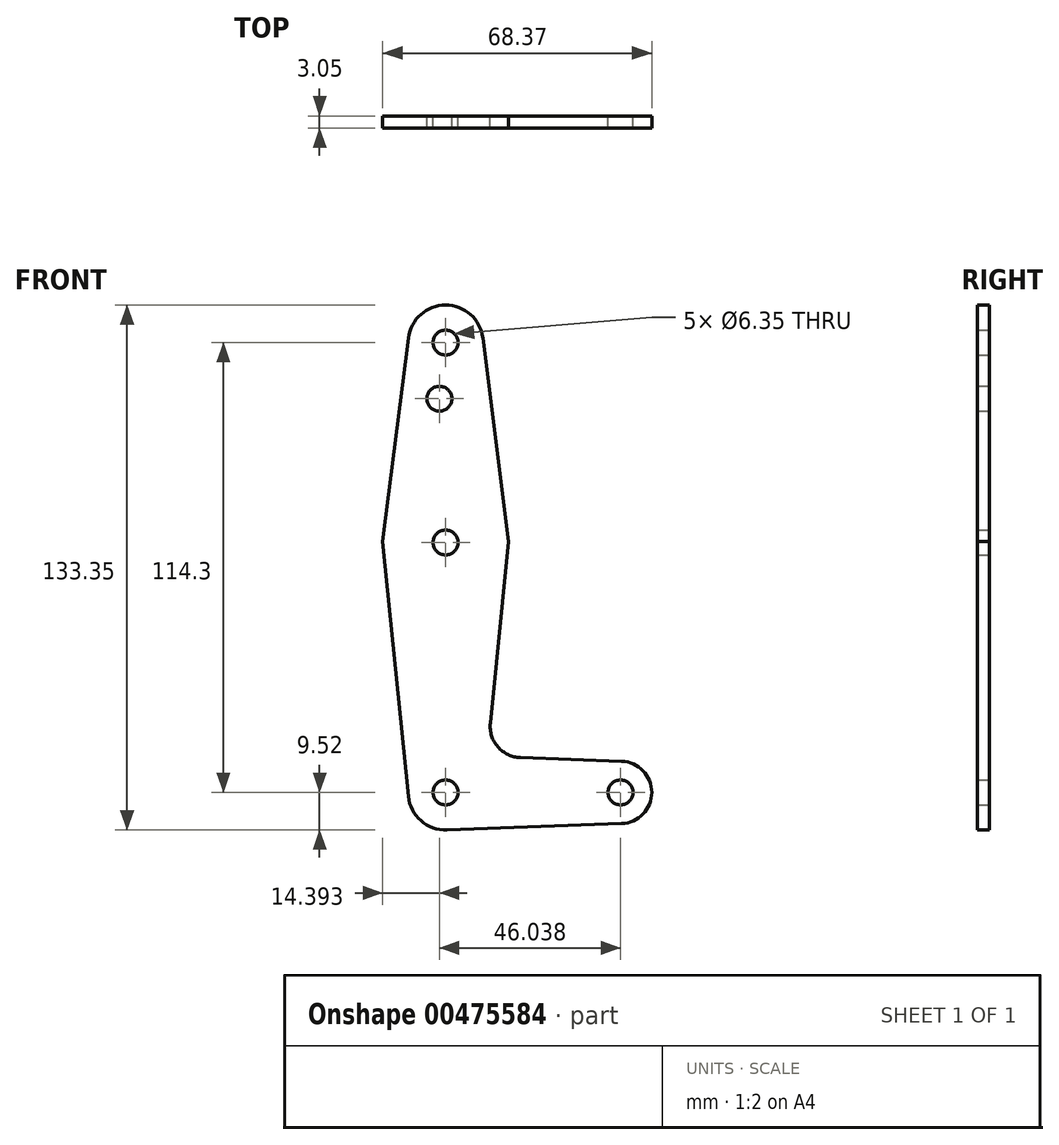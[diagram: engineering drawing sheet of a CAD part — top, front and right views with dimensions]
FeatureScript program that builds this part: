
annotation { "Feature Type Name" : "Feature", "Feature Type Description" : "" }
export const myFeature = defineFeature(function(context is Context, id is Id, definition is map)
    precondition{}
    {
        {
            var Q0;
            Q0=qCreatedBy(makeId("Front.planeOp"),FACE);
            var sketch = newSketch(context, id + "F0", { "sketchPlane" : qUnion([Q0])});
            skLineSegment(sketch, "E0", {"start": v(0, 0) * mm, "end": v(0, 114.3) * mm, "construction": true});
            skLineSegment(sketch, "E1", {"start": v(0, 0) * mm, "end": v(44.45, 0) * mm, "construction": true});
            skCircle(sketch, "E2", {"center": v(0, 114.3) * mm, "radius": 9.53 * mm});
            skCircle(sketch, "E3", {"center": v(0, 63.5) * mm, "radius": 15.88 * mm});
            skCircle(sketch, "E4", {"center": v(0, 0) * mm, "radius": 9.53 * mm});
            skCircle(sketch, "E5", {"center": v(44.45, 0) * mm, "radius": 7.94 * mm});
            skLineSegment(sketch, "E6", {"start": v(0.34, -9.52) * mm, "end": v(44.73, -7.93) * mm});
            skLineSegment(sketch, "E7", {"start": v(18.97, 8.85) * mm, "end": v(44.73, 7.93) * mm});
            skLineSegment(sketch, "E8", {"start": v(-15.98, 63.7) * mm, "end": v(-9.48, -0.95) * mm});
            skLineSegment(sketch, "E9", {"start": v(15.98, 63.7) * mm, "end": v(11.34, 17.6) * mm});
            skLineSegment(sketch, "E10", {"start": v(-9.45, 115.5) * mm, "end": v(-15.98, 63.7) * mm});
            skLineSegment(sketch, "E11", {"start": v(9.45, 115.5) * mm, "end": v(15.98, 63.7) * mm});
            skCircle(sketch, "E12", {"center": v(0, 114.3) * mm, "radius": 3.18 * mm});
            skCircle(sketch, "E13", {"center": v(0, 0) * mm, "radius": 3.18 * mm});
            skCircle(sketch, "E14", {"center": v(44.45, 0) * mm, "radius": 3.18 * mm});
            skArc(sketch, "E15.filletArc", {"start": v(11.34, 17.6) * mm, "mid": v(13.26, 11.57) * mm, "end": v(18.97, 8.85) * mm});
            skCircle(sketch, "E16", {"center": v(-1.59, 100.03) * mm, "radius": 3.18 * mm});
            skCircle(sketch, "E17", {"center": v(0, 63.5) * mm, "radius": 3.17 * mm});
            skSolve(sketch);
        }
        {
            var Q0;
            Q0 = qSketchRegion(id + "F0", true);
            extrude(context, id + "F1", {"entities" : qUnion([Q0]), "depth" : 3.05 * mm});
        }
    });
